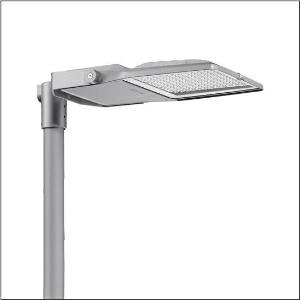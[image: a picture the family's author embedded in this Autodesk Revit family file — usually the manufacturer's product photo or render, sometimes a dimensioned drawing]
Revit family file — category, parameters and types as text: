
# Revit family: floodlight_fl_21_midi___pl43_5xa7786e2a3a_b253
name_source: partatom
category: Lighting Fixtures
units: mm (PartAtom-declared; Revit-internal decimal feet)

## family parameters
Cut with Voids When Loaded = No
Host = Face
Light Source = No
Part Type = Normal
Room Calculation Point = No
Round Connector Dimension = Use Diameter
Shared = No

## types (1)
- --- (1 x LED, 27640 lm, 212.4 W, 3000K)
    Apparent Load = 212 VA
    CIE Flux Codes = 27 78 99 100 100
    Color Rendering = 70
    Color Temperature = 3000K
    Default Elevation = 1800 mm
    Description = Floodlight FL 21 midi, floodlight, primary light control with lens, of PMMA, primary optical cover: protective disc, of toughened safety glass, transparent, light distribution: PL43, light emission: direct distribution, installation type: surface-mounted, LED, High Power LED, rated luminous flux: 27.640lm, luminous efficacy: 130lm/W, light colour: 730, colour temperature: 3000K, control gear: ECG Smart Interface, control: flexible luminous flux parameterisation, time-dependent luminous flux control, constant luminous flux control, overheat protection, pre-setting: logarithmic dimming characteristic, with terminal, 6-pole, mains connection: 220..240V, AC, 50/60Hz, start of lifetime: 212W, end of service life: 231W, reduction: 95W, luminaire housing, of diecast aluminium, powder-coated, Siteco® metallic grey (DB 702S), corrosivity category C5 mid according to DIN EN ISO 12944, sealing non-destructively replaceable, please order mast flange separately, mast bracket, of steel, galvanised, powder-coated, Siteco® metallic grey (DB 702S), Smart Interface below and above, protection rating (complete): IP66, insulation class (complete): insulation class II (safety insulation), certification: CE, ENEC, VDE, protection symbol: D, impact resistance: IK08, permissible operating ambient temperature: -40..+40°C, permissible operating ambient temperature for outdoor applications: -40..+50°C, standard: DIN EN 12944, LABS conformity tested according to VDMA 24364:2018-05, packaging unit: 1 piece

Light Distribution: PL43
    Height = 76 mm
    Lamp = 1 x LED
    Lamp Light Flux = 27640 lm
    Lamp Power = 212.4 W
    Lamp count = 1
    Length = 657 mm
    Luminous efficacy = 130 lm/W
    Manufacturer = Siteco
    ModVariant = No
    Model = 5XA7786E2A3A
    Number of Poles = 1
    OnlyDefault = Yes
    Power Factor = 1
    Product Name = Floodlight FL 21 midi | PL43
    Product group = floodlight | pylon annexe
    ProductGroupID = 6200
    Protection Class = Protection class II
    Protection Degree = IP 66
    RLX_Detail_Level = 1
    RLX_Emergency_Light_Flux = 0 lm
    RLX_Emergency_Type = 0
    RLX_Emergency_Type_DB = No
    RlxData = <blob elided: 153453 chars, md5=788dfd86>
    Socket = socket
    Standby Power = 0 W
    System Light Flux = 27640 lm
    System Power = 212 W
    Type Comments = factory setting: luminous flux: 100 % | dim-lin: 254 | 710 mA
    Type Image = l_1007123.jpg
    URL = http://relux.com
    VarID = @adj_148535
    Voltage = 0 V
    Weight = 0.00 kg
    Width = 442 mm

## geometry (parser evidence)
native form markers: Blend x4, Sweep x12
no freeform markers — native parametric forms only
